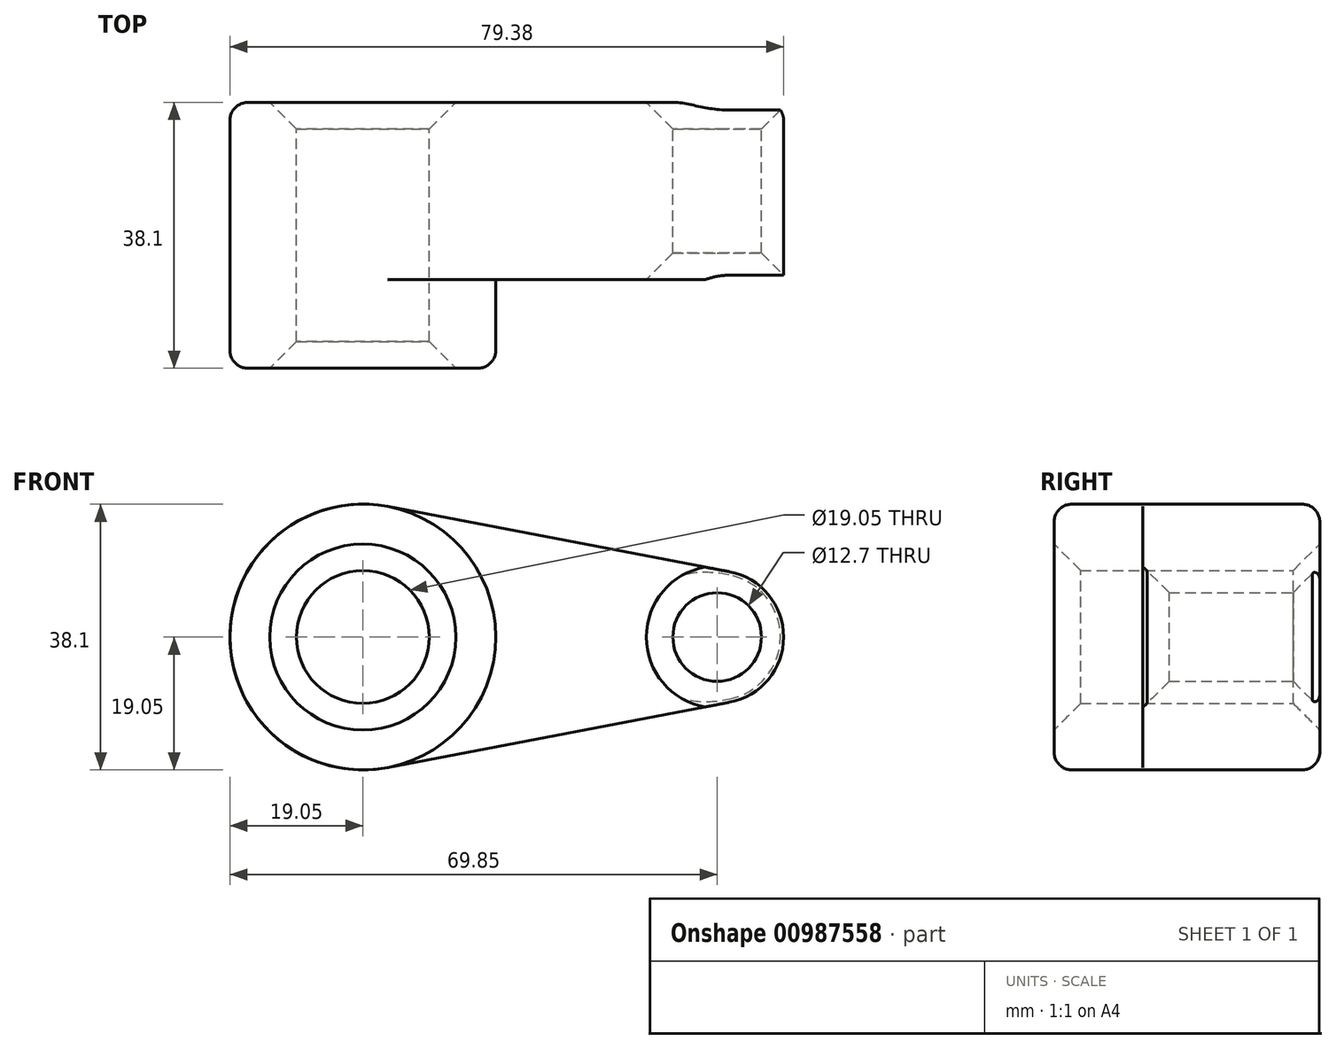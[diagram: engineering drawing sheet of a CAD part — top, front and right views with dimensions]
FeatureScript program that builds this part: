
annotation { "Feature Type Name" : "Feature", "Feature Type Description" : "" }
export const myFeature = defineFeature(function(context is Context, id is Id, definition is map)
    precondition{}
    {
        {
            var Q0;
            Q0=qCreatedBy(makeId("Front.planeOp"),FACE);
            var sketch = newSketch(context, id + "F0", { "sketchPlane" : qUnion([Q0])});
            skCircle(sketch, "E0", {"center": v(0, 0) * mm, "radius": 19.05 * mm});
            skCircle(sketch, "E1", {"center": v(50.8, 0) * mm, "radius": 9.53 * mm});
            skLineSegment(sketch, "E2", {"start": v(3.57, 18.71) * mm, "end": v(52.59, 9.36) * mm});
            skLineSegment(sketch, "E3", {"start": v(3.57, -18.71) * mm, "end": v(52.59, -9.36) * mm});
            skCircle(sketch, "E4", {"center": v(0, 0) * mm, "radius": 9.53 * mm});
            skCircle(sketch, "E5", {"center": v(50.8, 0) * mm, "radius": 6.35 * mm});
            skSolve(sketch);
        }
        {
            var Q0;
            Q0 = qSketchRegion(id + "F0", true);
            extrude(context, id + "F1", {"entities" : qUnion([Q0]), "depth" : 25.4 * mm, "offsetDistance" : 25.4 * mm});
        }
        {
            var Q0;
            Q0=makeQuery(id+"F0.imprint","IMPRINT",FACE,{"disambiguationData":[TD([[makeQuery(id+"F0.imprint","IMPRINT",EDGE,{"derivedFrom":sQuery(id+"F0.wireOp",EDGE,"E4")}),-1.0]])]});
            extrude(context, id + "F2", {"entities" : qUnion([Q0]), "operationType" : NewBodyOperationType.ADD, "depth" : 38.1 * mm, "offsetDistance" : 25.4 * mm});
        }
        {
            var Q0;
            Q0=makeQuery(id+"F1.opExtrude","CAP_EDGE",EDGE,{"disambiguationData":[OSD([sQuery(id+"F0.wireOp",EDGE,"E3")])],"isStart":true});
            var Q1;
            Q1=makeQuery(id+"F2.opExtrude","CAP_EDGE",EDGE,{"disambiguationData":[OSD([sQuery(id+"F0.wireOp",EDGE,"E0")])],"isStart":false});
            fillet(context, id + "F3", {"entities" : qUnion([Q0, Q1]), "radius" : 2.54 * mm, "tangentPropagation" : true, "allowEdgeOverflow" : false});
        }
        {
            var Q0;
            Q0=makeQuery(id+"F2.opExtrude","CAP_EDGE",EDGE,{"disambiguationData":[OSD([sQuery(id+"F0.wireOp",EDGE,"E4")])],"isStart":false});
            var Q1;
            Q1=makeQuery(id+"F1.opExtrude","CAP_EDGE",EDGE,{"disambiguationData":[OSD([sQuery(id+"F0.wireOp",EDGE,"E5")])],"isStart":false});
            var Q2;
            Q2=makeQuery(id+"F1.opExtrude","CAP_EDGE",EDGE,{"disambiguationData":[OSD([sQuery(id+"F0.wireOp",EDGE,"E4")])],"isStart":true});
            var Q3;
            Q3=makeQuery(id+"F1.opExtrude","CAP_EDGE",EDGE,{"disambiguationData":[OSD([sQuery(id+"F0.wireOp",EDGE,"E5")])],"isStart":true});
            chamfer(context, id + "F4", {"entities" : qUnion([Q0, Q1, Q2, Q3]), "width" : 3.8 * mm, "tangentPropagation" : true});
        }
    });
